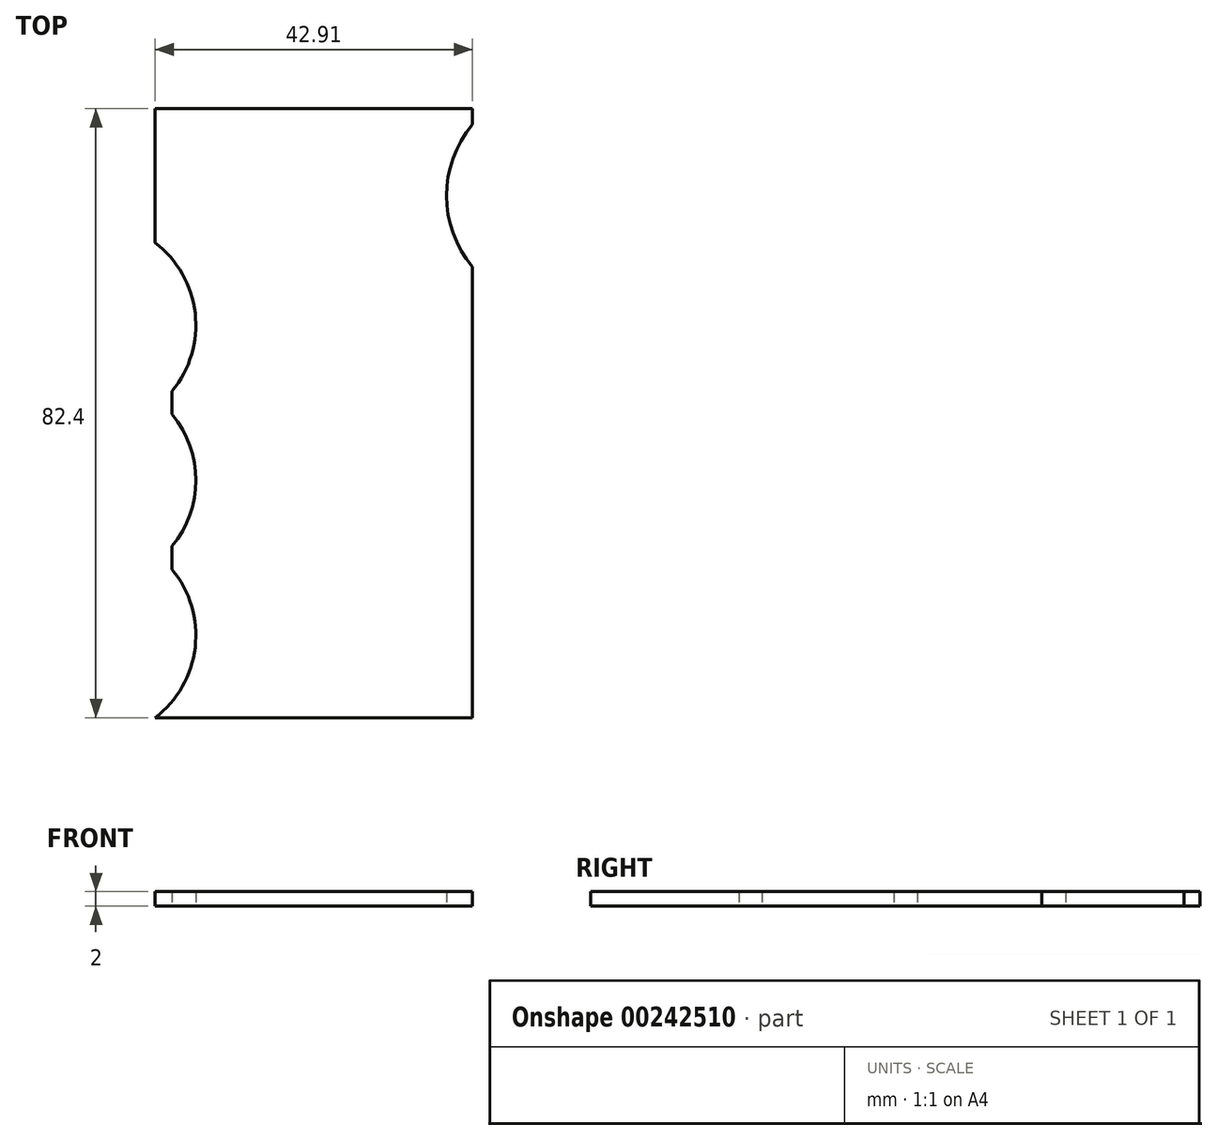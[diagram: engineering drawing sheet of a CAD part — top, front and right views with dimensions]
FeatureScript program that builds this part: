
annotation { "Feature Type Name" : "Feature", "Feature Type Description" : "" }
export const myFeature = defineFeature(function(context is Context, id is Id, definition is map)
    precondition{}
    {
        {
            var Q0;
            Q0=qCreatedBy(makeId("Top.planeOp"),FACE);
            var sketch = newSketch(context, id + "F0", { "sketchPlane" : qUnion([Q0])});
            skLineSegment(sketch, "E0.bottom", {"start": v(-23.48, 43.7) * mm, "end": v(19.43, 43.7) * mm});
            skPoint(sketch, "E0.middle", {"position": v(-21.77, -1.48) * mm});
            skArc(sketch, "E1.0", {"start": v(-23.48, 25.55) * mm, "mid": v(-18.07, 16.01) * mm, "end": v(-21.19, 5.5) * mm});
            skArc(sketch, "E1.1", {"start": v(-21.19, 2.34) * mm, "mid": v(-17.98, -6.58) * mm, "end": v(-21.19, -15.5) * mm});
            skArc(sketch, "E1.2", {"start": v(-21.19, -18.66) * mm, "mid": v(-18.07, -29.17) * mm, "end": v(-23.48, -38.7) * mm});
            skLineSegment(sketch, "E2", {"start": v(-23.48, 25.55) * mm, "end": v(-23.48, 43.7) * mm});
            skArc(sketch, "E3.0", {"start": v(19.43, 22.3) * mm, "mid": v(15.93, 31.92) * mm, "end": v(19.43, 41.55) * mm});
            skLineSegment(sketch, "E4", {"start": v(19.43, 41.55) * mm, "end": v(19.43, 43.7) * mm});
            skLineSegment(sketch, "E5", {"start": v(19.43, 22.3) * mm, "end": v(19.43, -38.7) * mm});
            skLineSegment(sketch, "E6", {"start": v(-21.19, -15.5) * mm, "end": v(-21.19, -18.66) * mm});
            skLineSegment(sketch, "E7", {"start": v(-21.19, 2.34) * mm, "end": v(-21.19, 5.5) * mm});
            skLineSegment(sketch, "E8", {"start": v(-23.48, -38.7) * mm, "end": v(19.43, -38.7) * mm});
            skSolve(sketch);
        }
        {
            var Q0;
            Q0 = qSketchRegion(id + "F0", true);
            extrude(context, id + "F1", {"entities" : qUnion([Q0]), "depth" : 2 * mm});
        }
    });
